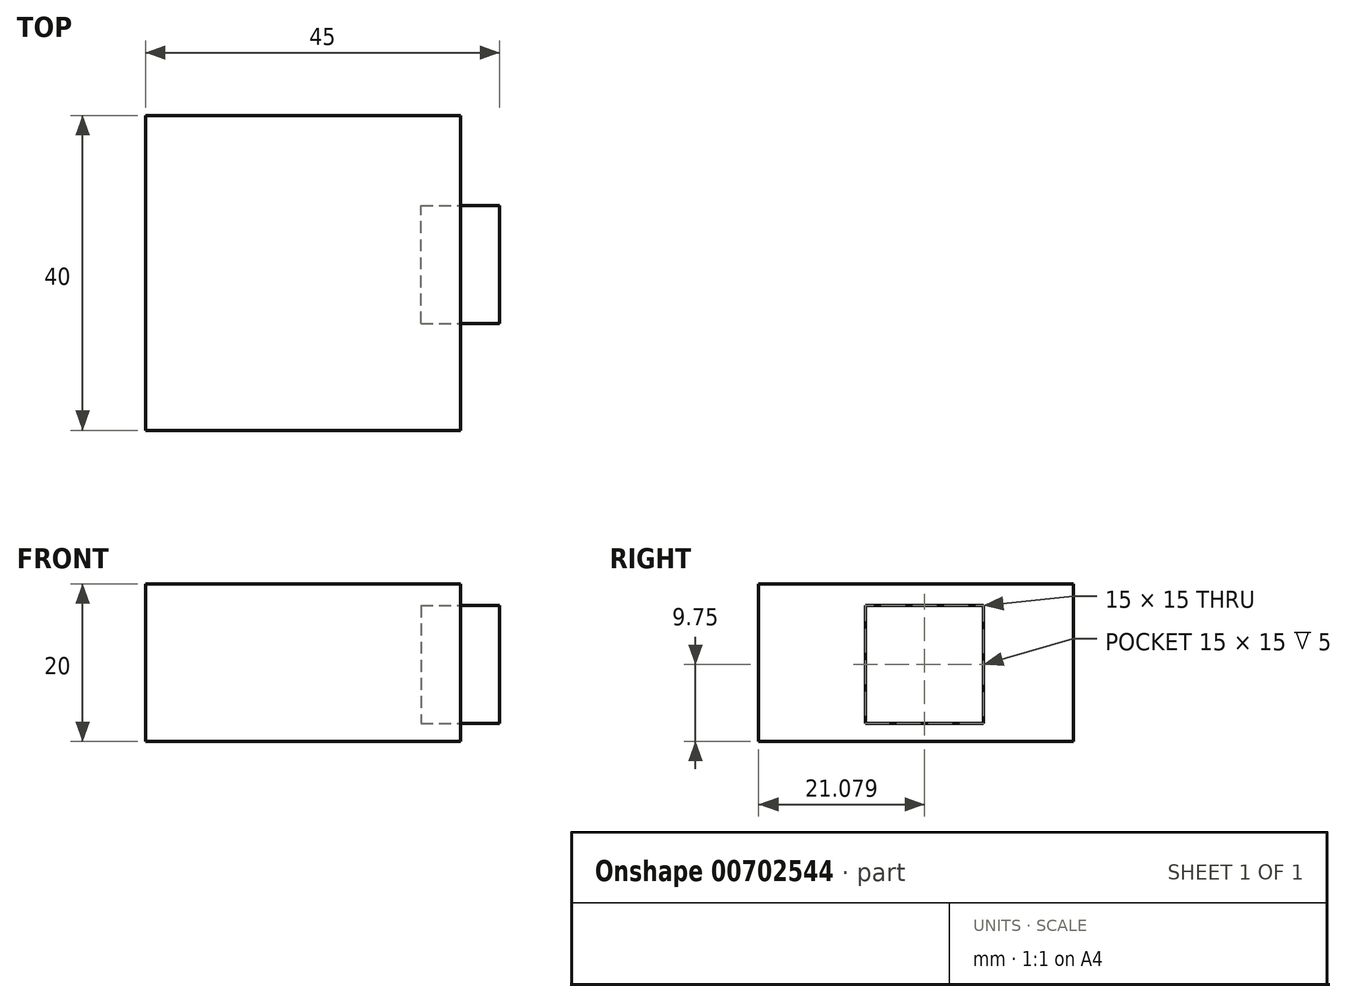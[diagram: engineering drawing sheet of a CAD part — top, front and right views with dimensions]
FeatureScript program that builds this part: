
annotation { "Feature Type Name" : "Feature", "Feature Type Description" : "" }
export const myFeature = defineFeature(function(context is Context, id is Id, definition is map)
    precondition{}
    {
        {
            var Q0;
            Q0=qCreatedBy(makeId("Top.planeOp"),FACE);
            var sketch = newSketch(context, id + "F0", { "sketchPlane" : qUnion([Q0])});
            skLineSegment(sketch, "E0.bottom", {"start": v(-45.13, 22.6) * mm, "end": v(-5.13, 22.6) * mm});
            skLineSegment(sketch, "E0.top", {"start": v(-45.13, -17.4) * mm, "end": v(-5.13, -17.4) * mm});
            skLineSegment(sketch, "E0.left", {"start": v(-45.13, 22.6) * mm, "end": v(-45.13, -17.4) * mm});
            skLineSegment(sketch, "E0.right", {"start": v(-5.13, 22.6) * mm, "end": v(-5.13, -17.4) * mm});
            skSolve(sketch);
        }
        {
            var Q0;
            Q0=makeQuery(id+"F0.imprint","IMPRINT",FACE,{"disambiguationData":[TD([[makeQuery(id+"F0.imprint","IMPRINT",EDGE,{"derivedFrom":sQuery(id+"F0.wireOp",EDGE,"E0.bottom")}),-1.0]])]});
            extrude(context, id + "F1", {"entities" : qUnion([Q0]), "depth" : 20 * mm, "offsetDistance" : 25 * mm});
        }
        {
            var Q0;
            Q0=makeQuery(id+"F1.opExtrude","SWEPT_FACE",FACE,{"disambiguationData":[OSD([sQuery(id+"F0.wireOp",EDGE,"E0.right")])]});
            var sketch = newSketch(context, id + "F2", { "sketchPlane" : qUnion([Q0])});
            skLineSegment(sketch, "E1.bottom", {"start": v(-3.83, 17.25) * mm, "end": v(11.17, 17.25) * mm});
            skLineSegment(sketch, "E1.top", {"start": v(-3.83, 2.25) * mm, "end": v(11.17, 2.25) * mm});
            skLineSegment(sketch, "E1.left", {"start": v(-3.83, 17.25) * mm, "end": v(-3.83, 2.25) * mm});
            skLineSegment(sketch, "E1.right", {"start": v(11.17, 17.25) * mm, "end": v(11.17, 2.25) * mm});
            skSolve(sketch);
        }
        {
            var Q0;
            Q0=makeQuery(id+"F1.opExtrude","SWEPT_BODY",BODY,{"disambiguationData":[OSD([sQuery(id+"F0.wireOp",EDGE,"E0.bottom"),sQuery(id+"F0.wireOp",EDGE,"E0.top"),sQuery(id+"F0.wireOp",EDGE,"E0.left"),sQuery(id+"F0.wireOp",EDGE,"E0.right")])]});
            transform(context, id + "F3", {"entities" : qUnion([Q0]), "transformType" : TransformType.TRANSLATION_3D, "dx" : 0 * mm, "dy" : 0 * mm, "dz" : 0 * mm, "makeCopy" : true});
        }
        {
            var Q0;
            Q0=makeQuery(id+"F2.imprint","IMPRINT",FACE,{"disambiguationData":[TD([[makeQuery(id+"F2.imprint","IMPRINT",EDGE,{"derivedFrom":sQuery(id+"F2.wireOp",EDGE,"E1.bottom")}),-1.0]])]});
            extrude(context, id + "F4", {"entities" : qUnion([Q0]), "depth" : 5 * mm, "offsetDistance" : 25 * mm});
        }
        {
            var Q0;
            Q0=makeQuery(id+"F3.opPattern","COPY",BODY,{"derivedFrom":makeQuery(id+"F1.opExtrude","SWEPT_BODY",BODY,{"disambiguationData":[OSD([sQuery(id+"F0.wireOp",EDGE,"E0.bottom"),sQuery(id+"F0.wireOp",EDGE,"E0.top"),sQuery(id+"F0.wireOp",EDGE,"E0.left"),sQuery(id+"F0.wireOp",EDGE,"E0.right")])]}),"instanceName":"1"});
            deleteBodies(context, id + "F5", {"entities" : qUnion([Q0])});
        }
        {
            var Q0;
            Q0=makeQuery(id+"F1.opExtrude","SWEPT_BODY",BODY,{"disambiguationData":[OSD([sQuery(id+"F0.wireOp",EDGE,"E0.bottom"),sQuery(id+"F0.wireOp",EDGE,"E0.top"),sQuery(id+"F0.wireOp",EDGE,"E0.left"),sQuery(id+"F0.wireOp",EDGE,"E0.right")])]});
            transform(context, id + "F6", {"entities" : qUnion([Q0]), "transformType" : TransformType.TRANSLATION_3D, "dx" : 0 * mm, "dy" : 0 * mm, "dz" : 0 * mm, "makeCopy" : true});
        }
        {
            var Q0;
            Q0=makeQuery(id+"F2.imprint","IMPRINT",FACE,{"disambiguationData":[TD([[makeQuery(id+"F2.imprint","IMPRINT",EDGE,{"derivedFrom":sQuery(id+"F2.wireOp",EDGE,"E1.bottom")}),-1.0]])]});
            extrude(context, id + "F7", {"entities" : qUnion([Q0]), "operationType" : NewBodyOperationType.REMOVE, "oppositeDirection" : true, "depth" : 5 * mm, "offsetDistance" : 25 * mm});
        }
    });
